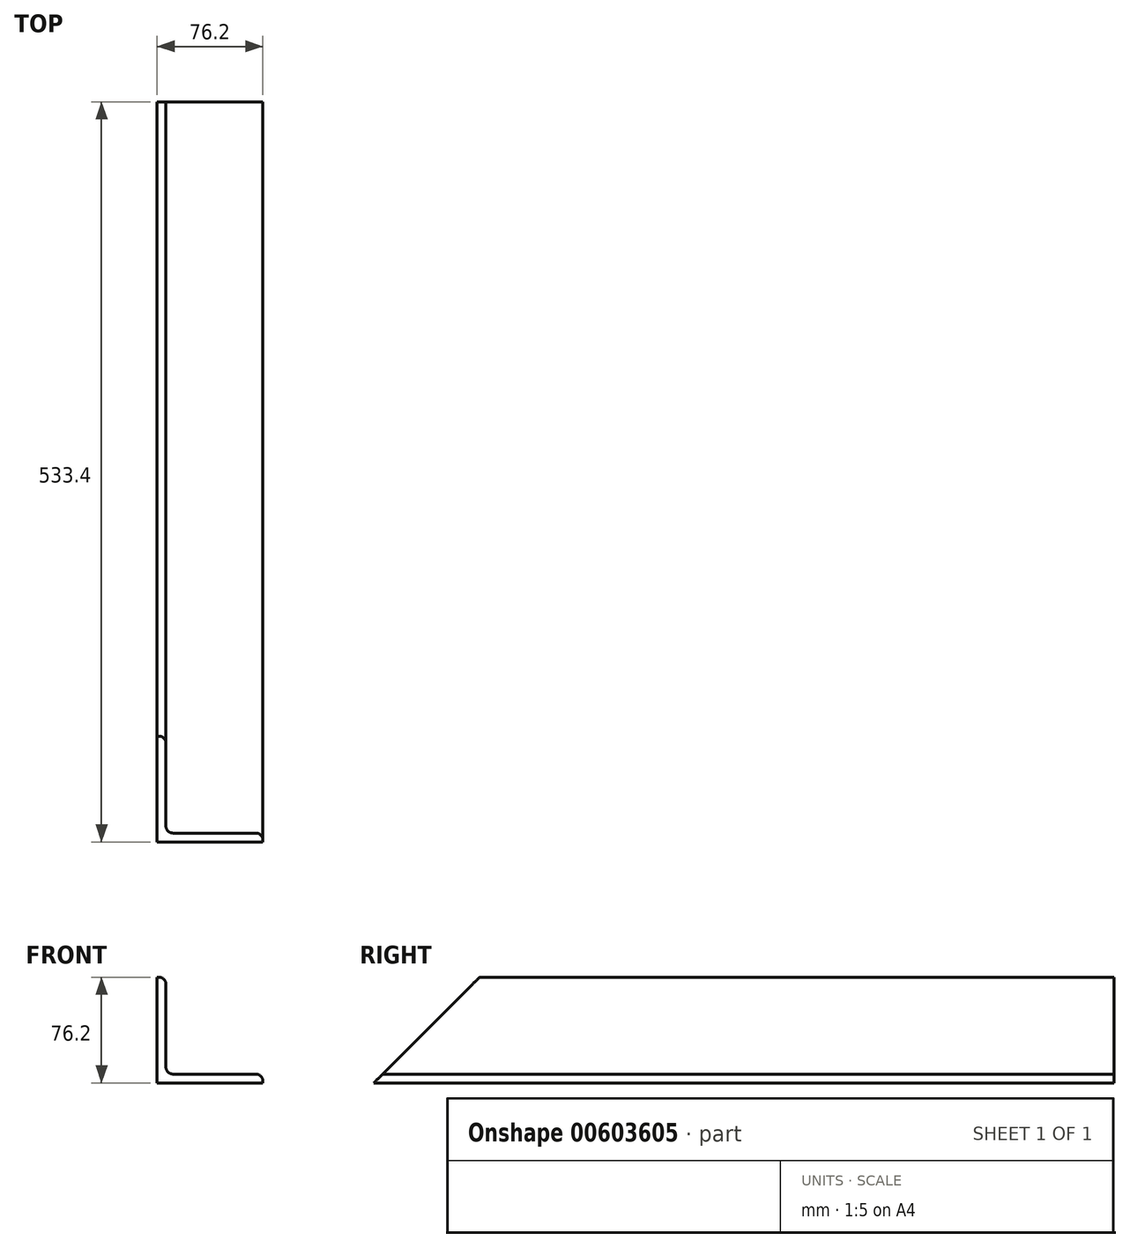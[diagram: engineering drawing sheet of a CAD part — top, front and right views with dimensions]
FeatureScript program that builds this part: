
annotation { "Feature Type Name" : "Feature", "Feature Type Description" : "" }
export const myFeature = defineFeature(function(context is Context, id is Id, definition is map)
    precondition{}
    {
        {
            var Q0;
            Q0=qCreatedBy(makeId("Front.planeOp"),FACE);
            var sketch = newSketch(context, id + "F0", { "sketchPlane" : qUnion([Q0])});
            skLineSegment(sketch, "E0.bottom", {"start": v(38.1, -38.1) * mm, "end": v(-38.1, -38.1) * mm});
            skLineSegment(sketch, "E0.top", {"start": v(-31.75, 38.1) * mm, "end": v(-38.1, 38.1) * mm});
            skLineSegment(sketch, "E0.left", {"start": v(38.1, -38.1) * mm, "end": v(38.1, -31.75) * mm});
            skLineSegment(sketch, "E0.right", {"start": v(-38.1, -38.1) * mm, "end": v(-38.1, 38.1) * mm});
            skPoint(sketch, "E0.middle", {"position": v(0, 0) * mm});
            skLineSegment(sketch, "E1.0", {"start": v(-31.75, -31.75) * mm, "end": v(-31.75, 38.1) * mm});
            skLineSegment(sketch, "E2.0", {"start": v(38.1, -31.75) * mm, "end": v(-31.75, -31.75) * mm});
            skPoint(sketch, "E3.orphan", {"position": v(38.1, 38.1) * mm});
            skSolve(sketch);
        }
        {
            var Q0;
            Q0 = qSketchRegion(id + "F0", true);
            extrude(context, id + "F1", {"entities" : qUnion([Q0]), "endBound" : BoundingType.SYMMETRIC, "depth" : 533.4 * mm, "offsetDistance" : 25.4 * mm});
        }
        {
            var Q0;
            Q0=makeQuery(id+"F1.opExtrude","SWEPT_EDGE",EDGE,{"disambiguationData":[OSD([sQuery(id+"F0.wireOp",EDGE,"E0.top"),sQuery(id+"F0.wireOp",EDGE,"E1.0")])]});
            var Q1;
            Q1=makeQuery(id+"F1.opExtrude","SWEPT_EDGE",EDGE,{"disambiguationData":[OSD([sQuery(id+"F0.wireOp",EDGE,"E1.0"),sQuery(id+"F0.wireOp",EDGE,"E2.0")])]});
            var Q2;
            Q2=makeQuery(id+"F1.opExtrude","SWEPT_EDGE",EDGE,{"disambiguationData":[OSD([sQuery(id+"F0.wireOp",EDGE,"E0.left"),sQuery(id+"F0.wireOp",EDGE,"E2.0")])]});
            fillet(context, id + "F2", {"entities" : qUnion([Q0, Q1, Q2]), "radius" : 5.08 * mm, "tangentPropagation" : true, "allowEdgeOverflow" : false});
        }
        {
            var Q0;
            Q0=makeQuery(id+"F1.opExtrude","SWEPT_FACE",FACE,{"disambiguationData":[OSD([sQuery(id+"F0.wireOp",EDGE,"E0.right")])]});
            var sketch = newSketch(context, id + "F3", { "sketchPlane" : qUnion([Q0])});
            skLineSegment(sketch, "E4", {"start": v(266.7, -38.1) * mm, "end": v(190.5, 38.1) * mm});
            skLineSegment(sketch, "E5", {"start": v(190.5, 38.1) * mm, "end": v(266.7, 38.1) * mm});
            skLineSegment(sketch, "E6", {"start": v(266.7, 38.1) * mm, "end": v(266.7, -38.1) * mm});
            skSolve(sketch);
        }
        {
            var Q0;
            Q0 = qSketchRegion(id + "F3", true);
            extrude(context, id + "F4", {"entities" : qUnion([Q0]), "operationType" : NewBodyOperationType.REMOVE, "oppositeDirection" : true, "depth" : 76.2 * mm, "offsetDistance" : 25.4 * mm});
        }
    });
